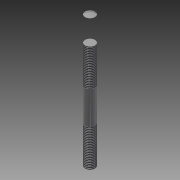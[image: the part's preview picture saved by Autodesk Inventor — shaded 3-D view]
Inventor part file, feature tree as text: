
AUTODESK INVENTOR PART (.ipt)
format: ipt  version: 2015 (Build 190159000, 159)  size: 108,544 bytes
history: native  units: mm
features: other x2, thread x2, sketch x2, extrude x1
ambient origin geometry x8: Origin, YZ Plane, XZ Plane, XY Plane, X Axis, Y Axis, Z Axis, Center Point
bodies: Body1 (feature_tree)
feature tree (7):
  other  "Bryła1"
  extrude  "Oś"  Depth=12.0mm
  thread  "Gwint1"
  thread  "Gwint2"
  other  "Obrót zakończeń"
  sketch  "Szkic1"
  sketch  "Szkic4"
